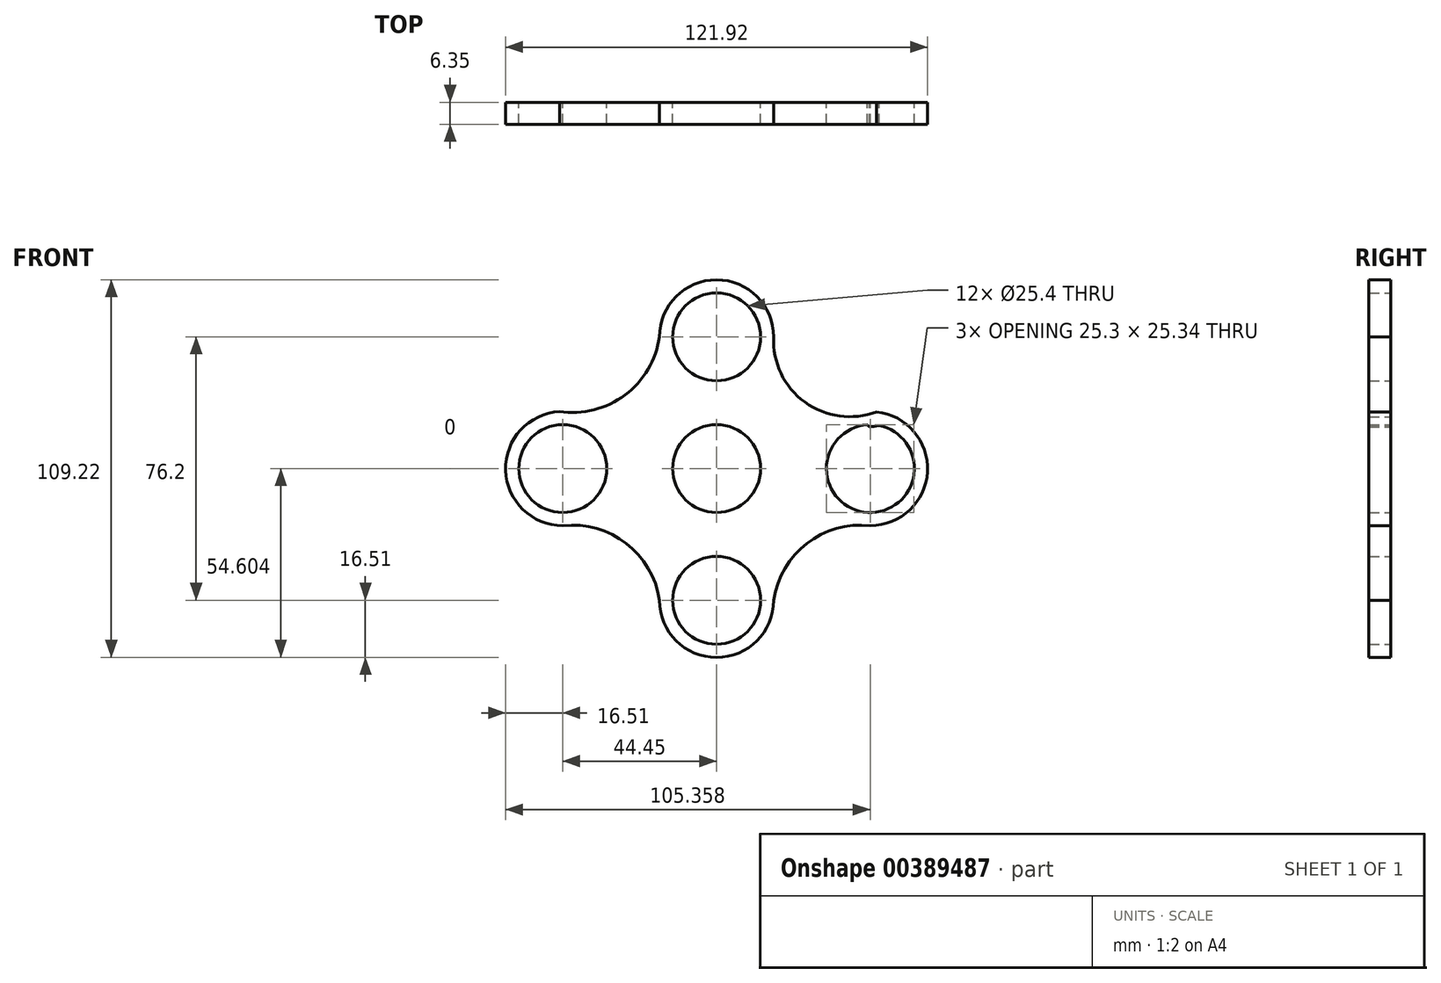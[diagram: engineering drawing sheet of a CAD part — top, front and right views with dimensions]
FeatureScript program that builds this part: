
annotation { "Feature Type Name" : "Feature", "Feature Type Description" : "" }
export const myFeature = defineFeature(function(context is Context, id is Id, definition is map)
    precondition{}
    {
        {
            var Q0;
            Q0=qCreatedBy(makeId("Front.planeOp"),FACE);
            var sketch = newSketch(context, id + "F0", { "sketchPlane" : qUnion([Q0])});
            skCircle(sketch, "E0", {"center": v(0, 0) * mm, "radius": 12.7 * mm});
            skArc(sketch, "E1", {"start": v(43.5, 12.66) * mm, "mid": v(43.69, -12.68) * mm, "end": v(46.92, 12.46) * mm});
            skCircle(sketch, "E2", {"center": v(0, 38.1) * mm, "radius": 16.51 * mm});
            skCircle(sketch, "E3", {"center": v(44.45, 0) * mm, "radius": 16.51 * mm});
            skCircle(sketch, "E4", {"center": v(0, -38.1) * mm, "radius": 16.51 * mm});
            skCircle(sketch, "E5", {"center": v(-44.45, 0) * mm, "radius": 16.51 * mm});
            skArc(sketch, "E6.trimOffspring", {"start": v(43.5, 12.66) * mm, "mid": v(43.84, 12.36) * mm, "end": v(44.2, 12.06) * mm});
            skPoint(sketch, "E7.orphan", {"position": v(31.75, 0) * mm});
            skPoint(sketch, "E8.orphan", {"position": v(0, -25.4) * mm});
            skPoint(sketch, "E9.orphan", {"position": v(-25.4, 0) * mm});
            skPoint(sketch, "E10.trimOffspring.end.orphan", {"position": v(0, 25.4) * mm});
            skPoint(sketch, "E11.end.orphan", {"position": v(-12.7, 38.1) * mm});
            skArc(sketch, "E12", {"start": v(-16.5, -38.1) * mm, "mid": v(-26.11, -21.66) * mm, "end": v(-44.45, -16.51) * mm});
            skArc(sketch, "E13", {"start": v(44.45, -16.51) * mm, "mid": v(26.11, -21.66) * mm, "end": v(16.51, -38.1) * mm});
            skPoint(sketch, "E14.start.orphan", {"position": v(-45.4, 12.66) * mm});
            skLineSegment(sketch, "E15", {"start": v(-45.4, 16.48) * mm, "end": v(-45.4, 16.48) * mm});
            skPoint(sketch, "E16.orphan", {"position": v(-16.5, 38.1) * mm});
            skCircle(sketch, "E17", {"center": v(-44.45, 0) * mm, "radius": 12.7 * mm});
            skArc(sketch, "E18", {"start": v(-45.4, 16.48) * mm, "mid": v(-26.45, 21.27) * mm, "end": v(-16.5, 38.1) * mm});
            skArc(sketch, "E19", {"start": v(16.5, 38.1) * mm, "mid": v(16.5, 37.8) * mm, "end": v(16.5, 37.52) * mm});
            skCircle(sketch, "E20.converted", {"center": v(0, 38.1) * mm, "radius": 12.7 * mm});
            skCircle(sketch, "E21.converted", {"center": v(0, -38.1) * mm, "radius": 12.7 * mm});
            skArc(sketch, "E22.trimOffspring", {"start": v(44.2, 12.06) * mm, "mid": v(45.56, 12.22) * mm, "end": v(46.92, 12.46) * mm});
            skPoint(sketch, "E23.orphan", {"position": v(56.37, 4.38) * mm});
            skPoint(sketch, "E24.trimOffspring.end.orphan", {"position": v(56.37, 16.48) * mm});
            skArc(sketch, "E25", {"start": v(16.5, 38.1) * mm, "mid": v(25.5, 19.23) * mm, "end": v(46.2, 16.42) * mm});
            skSolve(sketch);
        }
        {
            var Q0;
            Q0=makeQuery(id+"F0.imprint","IMPRINT",FACE,{"disambiguationData":[TD([[makeQuery(id+"F0.imprint","IMPRINT",EDGE,{"derivedFrom":sQuery(id+"F0.wireOp",EDGE,"E0")}),-1.0]])]});
            var Q1;
            {var subQ0=sQuery(id+"F0.wireOp",EDGE,"SUILtcg7-9WHF-f6VP-AZv6-ERQTraqNa5ZM");var subQ1=sQuery(id+"F0.wireOp",EDGE,"E11");var subQ2=makeQuery(id+"F0.imprint","INTERSECT",VERTEX,{"derivedFrom":[subQ1,subQ0]});Q1=makeQuery(id+"F0.imprint","IMPRINT",FACE,{"disambiguationData":[TD([[makeQuery(id+"F0.imprint","IMPRINT",EDGE,{"disambiguationData":[TD([[subQ2,-1.0]])],"derivedFrom":subQ1}),-1.0]])]});}
            var Q2;
            {var subQ3=sQuery(id+"F0.wireOp",EDGE,"E11");var subQ5=sQuery(id+"F0.wireOp",EDGE,"E2");var subQ7=makeQuery(id+"F0.imprint","INTERSECT",VERTEX,{"derivedFrom":[subQ3,subQ5]});Q2=makeQuery(id+"F0.imprint","IMPRINT",FACE,{"disambiguationData":[TD([[makeQuery(id+"F0.imprint","IMPRINT",EDGE,{"disambiguationData":[TD([[subQ7,-1.0]])],"derivedFrom":subQ3}),-1.0]])]});}
            var Q3;
            {var subQ1=sQuery(id+"F0.wireOp",EDGE,"ABrLUrjz-xXpH-Pjqi-05zA-Y5cuc3cMGpO4");var subQ3=sQuery(id+"F0.wireOp",EDGE,"E2");var subQ4=makeQuery(id+"F0.imprint","INTERSECT",VERTEX,{"derivedFrom":[subQ1,subQ3]});Q3=makeQuery(id+"F0.imprint","IMPRINT",FACE,{"disambiguationData":[TD([[makeQuery(id+"F0.imprint","IMPRINT",EDGE,{"disambiguationData":[TD([[subQ4,1.0]])],"derivedFrom":subQ3}),1.0]])]});}
            var Q4;
            {var subQ3=sQuery(id+"F0.wireOp",EDGE,"Qb0eh5pC-mcBY-aky9-Ua7v-p1ffr0VBUA6w");var subQ5=sQuery(id+"F0.wireOp",EDGE,"E2");var subQ6=makeQuery(id+"F0.imprint","INTERSECT",VERTEX,{"derivedFrom":[subQ3,subQ5]});Q4=makeQuery(id+"F0.imprint","IMPRINT",FACE,{"disambiguationData":[TD([[makeQuery(id+"F0.imprint","IMPRINT",EDGE,{"disambiguationData":[TD([[subQ6,1.0]])],"derivedFrom":subQ3}),-1.0]])]});}
            var Q5;
            {var subQ0=sQuery(id+"F0.wireOp",EDGE,"Qb0eh5pC-mcBY-aky9-Ua7v-p1ffr0VBUA6w");var subQ1=sQuery(id+"F0.wireOp",EDGE,"LB7PhWsd-VlXF-3D4b-IQIx-ij0umwf7cvhy");var subQ2=makeQuery(id+"F0.imprint","INTERSECT",VERTEX,{"disambiguationData":[OD(0.0)],"derivedFrom":[subQ1,subQ0]});Q5=makeQuery(id+"F0.imprint","IMPRINT",FACE,{"disambiguationData":[TD([[makeQuery(id+"F0.imprint","IMPRINT",EDGE,{"disambiguationData":[TD([[subQ2,-1.0]])],"derivedFrom":subQ1}),-1.0]])]});}
            var Q6;
            {var subQ0=sQuery(id+"F0.wireOp",EDGE,"E2");var subQ1=sQuery(id+"F0.wireOp",EDGE,"Qb0eh5pC-mcBY-aky9-Ua7v-p1ffr0VBUA6w");var subQ2=makeQuery(id+"F0.imprint","INTERSECT",VERTEX,{"derivedFrom":[subQ1,subQ0]});Q6=makeQuery(id+"F0.imprint","IMPRINT",FACE,{"disambiguationData":[TD([[makeQuery(id+"F0.imprint","IMPRINT",EDGE,{"disambiguationData":[TD([[subQ2,-1.0]])],"derivedFrom":subQ1}),-1.0]])]});}
            var Q7;
            {var subQ0=sQuery(id+"F0.wireOp",EDGE,"ABrLUrjz-xXpH-Pjqi-05zA-Y5cuc3cMGpO4");var subQ1=sQuery(id+"F0.wireOp",EDGE,"Qb0eh5pC-mcBY-aky9-Ua7v-p1ffr0VBUA6w");var subQ2=makeQuery(id+"F0.imprint","INTERSECT",VERTEX,{"derivedFrom":[subQ1,subQ0]});Q7=makeQuery(id+"F0.imprint","IMPRINT",FACE,{"disambiguationData":[TD([[makeQuery(id+"F0.imprint","IMPRINT",EDGE,{"disambiguationData":[TD([[subQ2,-1.0]])],"derivedFrom":subQ1}),1.0]])]});}
            var Q8;
            {var subQ1=sQuery(id+"F0.wireOp",EDGE,"E1");var subQ3=sQuery(id+"F0.wireOp",EDGE,"ABrLUrjz-xXpH-Pjqi-05zA-Y5cuc3cMGpO4");var subQ4=makeQuery(id+"F0.imprint","INTERSECT",VERTEX,{"derivedFrom":[subQ1,subQ3]});Q8=makeQuery(id+"F0.imprint","IMPRINT",FACE,{"disambiguationData":[TD([[makeQuery(id+"F0.imprint","IMPRINT",EDGE,{"disambiguationData":[TD([[subQ4,1.0]])],"derivedFrom":subQ3}),-1.0]])]});}
            var Q9;
            {var subQ1=sQuery(id+"F0.wireOp",EDGE,"Qb0eh5pC-mcBY-aky9-Ua7v-p1ffr0VBUA6w");var subQ3=sQuery(id+"F0.wireOp",EDGE,"E3");var subQ4=makeQuery(id+"F0.imprint","INTERSECT",VERTEX,{"derivedFrom":[subQ1,subQ3]});Q9=makeQuery(id+"F0.imprint","IMPRINT",FACE,{"disambiguationData":[TD([[makeQuery(id+"F0.imprint","IMPRINT",EDGE,{"disambiguationData":[TD([[subQ4,-1.0]])],"derivedFrom":subQ3}),1.0]])]});}
            var Q10;
            {var subQ3=sQuery(id+"F0.wireOp",EDGE,"3HJjQVQJ-BHby-ThzN-sahe-j0xexLQNlhHO");var subQ5=sQuery(id+"F0.wireOp",EDGE,"E3");var subQ7=makeQuery(id+"F0.imprint","INTERSECT",VERTEX,{"derivedFrom":[subQ3,subQ5]});Q10=makeQuery(id+"F0.imprint","IMPRINT",FACE,{"disambiguationData":[TD([[makeQuery(id+"F0.imprint","IMPRINT",EDGE,{"disambiguationData":[TD([[subQ7,1.0]])],"derivedFrom":subQ3}),-1.0]])]});}
            var Q11;
            {var subQ0=sQuery(id+"F0.wireOp",EDGE,"3HJjQVQJ-BHby-ThzN-sahe-j0xexLQNlhHO");var subQ1=sQuery(id+"F0.wireOp",EDGE,"Y8aUpacR-f0DI-SImS-VqXk-MbdZgQlNfAHo");var subQ2=makeQuery(id+"F0.imprint","INTERSECT",VERTEX,{"derivedFrom":[subQ1,subQ0]});Q11=makeQuery(id+"F0.imprint","IMPRINT",FACE,{"disambiguationData":[TD([[makeQuery(id+"F0.imprint","IMPRINT",EDGE,{"disambiguationData":[TD([[subQ2,1.0]])],"derivedFrom":subQ1}),1.0]])]});}
            var Q12;
            {var subQ1=sQuery(id+"F0.wireOp",EDGE,"E1");var subQ5=makeQuery(id+"F0.imprint","IMPRINT",VERTEX,{"derivedFrom":subQ1});Q12=makeQuery(id+"F0.imprint","IMPRINT",FACE,{"disambiguationData":[TD([[makeQuery(id+"F0.imprint","IMPRINT",EDGE,{"disambiguationData":[TD([[subQ5,-1.0]])],"derivedFrom":subQ1}),-1.0]])]});}
            var Q13;
            {var subQ0=sQuery(id+"F0.wireOp",EDGE,"3HJjQVQJ-BHby-ThzN-sahe-j0xexLQNlhHO");var subQ1=sQuery(id+"F0.wireOp",EDGE,"Y8aUpacR-f0DI-SImS-VqXk-MbdZgQlNfAHo");var subQ2=makeQuery(id+"F0.imprint","INTERSECT",VERTEX,{"derivedFrom":[subQ1,subQ0]});Q13=makeQuery(id+"F0.imprint","IMPRINT",FACE,{"disambiguationData":[TD([[makeQuery(id+"F0.imprint","IMPRINT",EDGE,{"disambiguationData":[TD([[subQ2,-1.0]])],"derivedFrom":subQ1}),-1.0]])]});}
            var Q14;
            {var subQ3=sQuery(id+"F0.wireOp",EDGE,"Y8aUpacR-f0DI-SImS-VqXk-MbdZgQlNfAHo");var subQ5=sQuery(id+"F0.wireOp",EDGE,"E4");var subQ7=makeQuery(id+"F0.imprint","INTERSECT",VERTEX,{"derivedFrom":[subQ3,subQ5]});Q14=makeQuery(id+"F0.imprint","IMPRINT",FACE,{"disambiguationData":[TD([[makeQuery(id+"F0.imprint","IMPRINT",EDGE,{"disambiguationData":[TD([[subQ7,-1.0]])],"derivedFrom":subQ3}),-1.0]])]});}
            var Q15;
            {var subQ1=sQuery(id+"F0.wireOp",EDGE,"6l55p9PR-ZDXd-e0ij-miTY-WXjTskL67P6R");var subQ5=sQuery(id+"F0.wireOp",EDGE,"Y8aUpacR-f0DI-SImS-VqXk-MbdZgQlNfAHo");var subQ6=makeQuery(id+"F0.imprint","INTERSECT",VERTEX,{"disambiguationData":[OD(0.0)],"derivedFrom":[subQ1,subQ5]});Q15=makeQuery(id+"F0.imprint","IMPRINT",FACE,{"disambiguationData":[TD([[makeQuery(id+"F0.imprint","IMPRINT",EDGE,{"disambiguationData":[TD([[subQ6,-1.0]])],"derivedFrom":subQ1}),-1.0]])]});}
            var Q16;
            {var subQ0=sQuery(id+"F0.wireOp",EDGE,"Tat4e3nz-2zsg-jR3U-NWRX-35KgbjdX1e69");var subQ1=sQuery(id+"F0.wireOp",EDGE,"0ZYXZZAd-Z4RQ-WgqZ-Elk1-BltrpxiTG6aJ");var subQ2=makeQuery(id+"F0.imprint","INTERSECT",VERTEX,{"derivedFrom":[subQ1,subQ0]});Q16=makeQuery(id+"F0.imprint","IMPRINT",FACE,{"disambiguationData":[TD([[makeQuery(id+"F0.imprint","IMPRINT",EDGE,{"disambiguationData":[TD([[subQ2,1.0]])],"derivedFrom":subQ1}),1.0]])]});}
            var Q17;
            {var subQ1=sQuery(id+"F0.wireOp",EDGE,"6l55p9PR-ZDXd-e0ij-miTY-WXjTskL67P6R");var subQ3=sQuery(id+"F0.wireOp",EDGE,"Tat4e3nz-2zsg-jR3U-NWRX-35KgbjdX1e69");var subQ4=makeQuery(id+"F0.imprint","INTERSECT",VERTEX,{"derivedFrom":[subQ1,subQ3]});Q17=makeQuery(id+"F0.imprint","IMPRINT",FACE,{"disambiguationData":[TD([[makeQuery(id+"F0.imprint","IMPRINT",EDGE,{"disambiguationData":[TD([[subQ4,-1.0]])],"derivedFrom":subQ3}),-1.0]])]});}
            var Q18;
            {var subQ0=sQuery(id+"F0.wireOp",EDGE,"Tat4e3nz-2zsg-jR3U-NWRX-35KgbjdX1e69");var subQ1=sQuery(id+"F0.wireOp",EDGE,"0ZYXZZAd-Z4RQ-WgqZ-Elk1-BltrpxiTG6aJ");var subQ2=makeQuery(id+"F0.imprint","INTERSECT",VERTEX,{"derivedFrom":[subQ1,subQ0]});Q18=makeQuery(id+"F0.imprint","IMPRINT",FACE,{"disambiguationData":[TD([[makeQuery(id+"F0.imprint","IMPRINT",EDGE,{"disambiguationData":[TD([[subQ2,-1.0]])],"derivedFrom":subQ1}),-1.0]])]});}
            var Q19;
            {var subQ1=sQuery(id+"F0.wireOp",EDGE,"E11");var subQ3=sQuery(id+"F0.wireOp",EDGE,"E5");var subQ4=makeQuery(id+"F0.imprint","INTERSECT",VERTEX,{"derivedFrom":[subQ1,subQ3]});Q19=makeQuery(id+"F0.imprint","IMPRINT",FACE,{"disambiguationData":[TD([[makeQuery(id+"F0.imprint","IMPRINT",EDGE,{"disambiguationData":[TD([[subQ4,1.0]])],"derivedFrom":subQ3}),1.0]])]});}
            var Q20;
            {var subQ0=sQuery(id+"F0.wireOp",EDGE,"SUILtcg7-9WHF-f6VP-AZv6-ERQTraqNa5ZM");var subQ1=sQuery(id+"F0.wireOp",EDGE,"E11");var subQ2=makeQuery(id+"F0.imprint","INTERSECT",VERTEX,{"derivedFrom":[subQ1,subQ0]});Q20=makeQuery(id+"F0.imprint","IMPRINT",FACE,{"disambiguationData":[TD([[makeQuery(id+"F0.imprint","IMPRINT",EDGE,{"disambiguationData":[TD([[subQ2,1.0]])],"derivedFrom":subQ1}),1.0]])]});}
            var Q21;
            {var subQ3=sQuery(id+"F0.wireOp",EDGE,"SUILtcg7-9WHF-f6VP-AZv6-ERQTraqNa5ZM");var subQ5=sQuery(id+"F0.wireOp",EDGE,"E5");var subQ6=makeQuery(id+"F0.imprint","INTERSECT",VERTEX,{"derivedFrom":[subQ3,subQ5]});Q21=makeQuery(id+"F0.imprint","IMPRINT",FACE,{"disambiguationData":[TD([[makeQuery(id+"F0.imprint","IMPRINT",EDGE,{"disambiguationData":[TD([[subQ6,1.0]])],"derivedFrom":subQ3}),-1.0]])]});}
            var Q22;
            {var subQ3=sQuery(id+"F0.wireOp",EDGE,"0ZYXZZAd-Z4RQ-WgqZ-Elk1-BltrpxiTG6aJ");var subQ5=sQuery(id+"F0.wireOp",EDGE,"E5");var subQ6=makeQuery(id+"F0.imprint","INTERSECT",VERTEX,{"derivedFrom":[subQ3,subQ5]});Q22=makeQuery(id+"F0.imprint","IMPRINT",FACE,{"disambiguationData":[TD([[makeQuery(id+"F0.imprint","IMPRINT",EDGE,{"disambiguationData":[TD([[subQ6,-1.0]])],"derivedFrom":subQ3}),-1.0]])]});}
            var Q23;
            {var subQ1=sQuery(id+"F0.wireOp",EDGE,"SUILtcg7-9WHF-f6VP-AZv6-ERQTraqNa5ZM");var subQ3=sQuery(id+"F0.wireOp",EDGE,"wMchlmK9-UfT7-xgjK-jumE-nHbJCgH0wGLG");var subQ8=makeQuery(id+"F0.imprint","INTERSECT",VERTEX,{"disambiguationData":[OD(0.0)],"derivedFrom":[subQ3,subQ1]});Q23=makeQuery(id+"F0.imprint","IMPRINT",FACE,{"disambiguationData":[TD([[makeQuery(id+"F0.imprint","IMPRINT",EDGE,{"disambiguationData":[TD([[subQ8,1.0]])],"derivedFrom":subQ3}),-1.0]])]});}
            var Q24;
            {var subQ2=sQuery(id+"F0.wireOp",EDGE,"E15");Q24=makeQuery(id+"F0.imprint","IMPRINT",FACE,{"disambiguationData":[TD([[makeQuery(id+"F0.imprint","IMPRINT",EDGE,{"derivedFrom":subQ2}),-1.0]])]});}
            var Q25;
            Q25=makeQuery(id+"F0.imprint","IMPRINT",FACE,{"disambiguationData":[TD([[makeQuery(id+"F0.imprint","IMPRINT",EDGE,{"derivedFrom":sQuery(id+"F0.wireOp",EDGE,"E21.converted")}),-1.0]])]});
            var Q26;
            Q26=sQuery(id+"F0.wireOp",EDGE,"E2");
            var Q27;
            Q27=sQuery(id+"F0.wireOp",EDGE,"E3");
            var Q28;
            Q28=sQuery(id+"F0.wireOp",EDGE,"E4");
            var Q29;
            Q29=sQuery(id+"F0.wireOp",EDGE,"E0");
            var Q30;
            Q30=sQuery(id+"F0.wireOp",EDGE,"LB7PhWsd-VlXF-3D4b-IQIx-ij0umwf7cvhy");
            var Q31;
            Q31=sQuery(id+"F0.wireOp",EDGE,"E1");
            var Q32;
            Q32=sQuery(id+"F0.wireOp",EDGE,"6l55p9PR-ZDXd-e0ij-miTY-WXjTskL67P6R");
            var Q33;
            Q33=sQuery(id+"F0.wireOp",EDGE,"wMchlmK9-UfT7-xgjK-jumE-nHbJCgH0wGLG");
            var Q34;
            Q34=sQuery(id+"F0.wireOp",EDGE,"Qb0eh5pC-mcBY-aky9-Ua7v-p1ffr0VBUA6w");
            var Q35;
            Q35=sQuery(id+"F0.wireOp",EDGE,"ABrLUrjz-xXpH-Pjqi-05zA-Y5cuc3cMGpO4");
            var Q36;
            Q36=sQuery(id+"F0.wireOp",EDGE,"E11");
            var Q37;
            Q37=sQuery(id+"F0.wireOp",EDGE,"SUILtcg7-9WHF-f6VP-AZv6-ERQTraqNa5ZM");
            var Q38;
            Q38=sQuery(id+"F0.wireOp",EDGE,"0ZYXZZAd-Z4RQ-WgqZ-Elk1-BltrpxiTG6aJ");
            var Q39;
            Q39=sQuery(id+"F0.wireOp",EDGE,"Tat4e3nz-2zsg-jR3U-NWRX-35KgbjdX1e69");
            var Q40;
            Q40=sQuery(id+"F0.wireOp",EDGE,"Y8aUpacR-f0DI-SImS-VqXk-MbdZgQlNfAHo");
            var Q41;
            Q41=sQuery(id+"F0.wireOp",EDGE,"3HJjQVQJ-BHby-ThzN-sahe-j0xexLQNlhHO");
            var Q42;
            Q42=sQuery(id+"F0.wireOp",EDGE,"E5");
            extrude(context, id + "F1", {"entities" : qUnion([Q0, Q1, Q2, Q3, Q4, Q5, Q6, Q7, Q8, Q9, Q10, Q11, Q12, Q13, Q14, Q15, Q16, Q17, Q18, Q19, Q20, Q21, Q22, Q23, Q24, Q25]), "surfaceEntities" : qUnion([Q26, Q27, Q28, Q29, Q30, Q31, Q32, Q33, Q34, Q35, Q36, Q37, Q38, Q39, Q40, Q41, Q42]), "depth" : 6.35 * mm});
        }
    });
